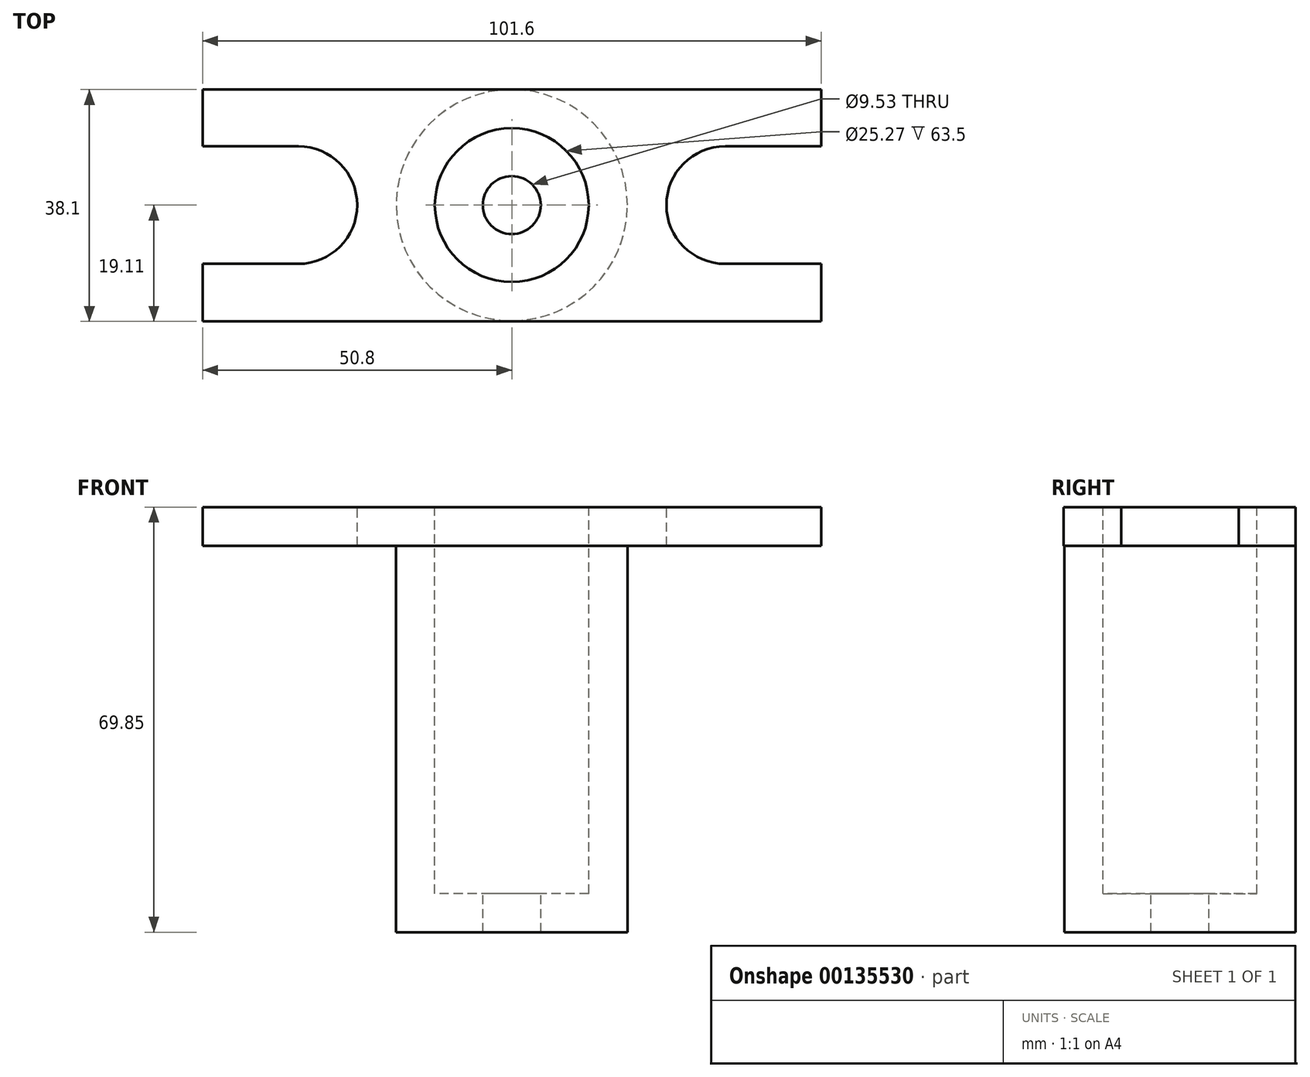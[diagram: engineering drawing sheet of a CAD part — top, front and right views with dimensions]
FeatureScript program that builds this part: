
annotation { "Feature Type Name" : "Feature", "Feature Type Description" : "" }
export const myFeature = defineFeature(function(context is Context, id is Id, definition is map)
    precondition{}
    {
        {
            var Q0;
            Q0=qCreatedBy(makeId("Front.planeOp"),FACE);
            var sketch = newSketch(context, id + "F0", { "sketchPlane" : qUnion([Q0])});
            skLineSegment(sketch, "E0", {"start": v(4.76, 0) * mm, "end": v(18.99, 0) * mm});
            skLineSegment(sketch, "E1", {"start": v(18.99, 0) * mm, "end": v(18.99, 63.5) * mm});
            skLineSegment(sketch, "E2", {"start": v(18.99, 63.5) * mm, "end": v(12.64, 63.5) * mm});
            skLineSegment(sketch, "E3", {"start": v(12.64, 63.5) * mm, "end": v(12.64, 6.35) * mm});
            skLineSegment(sketch, "E4", {"start": v(12.64, 6.35) * mm, "end": v(4.76, 6.35) * mm});
            skLineSegment(sketch, "E5", {"start": v(4.76, 6.35) * mm, "end": v(4.76, 0) * mm});
            skLineSegment(sketch, "E6", {"start": v(0, 37.58) * mm, "end": v(0, -25.7) * mm, "construction": true});
            skSolve(sketch);
        }
        {
            var Q0;
            Q0=makeQuery(id+"F0.imprint","IMPRINT",FACE,{"disambiguationData":[TD([[makeQuery(id+"F0.imprint","IMPRINT",EDGE,{"derivedFrom":sQuery(id+"F0.wireOp",EDGE,"E0")}),1.0]])]});
            var Q1;
            Q1=sQuery(id+"F0.wireOp",EDGE,"E6");
            revolve(context, id + "F1", {"entities" : qUnion([Q0]), "axis" : qUnion([Q1]), "revolveType" : RevolveType.FULL});
        }
        {
            var Q0;
            Q0=makeQuery(id+"F1.opRevolve","SWEPT_FACE",FACE,{"disambiguationData":[OSD([sQuery(id+"F0.wireOp",EDGE,"E2")])]});
            var sketch = newSketch(context, id + "F2", { "sketchPlane" : qUnion([Q0])});
            skLineSegment(sketch, "E7", {"start": v(0, -18.99) * mm, "end": v(0, 49.89) * mm});
            skLineSegment(sketch, "E8", {"start": v(0, 49.89) * mm, "end": v(0, 18.99) * mm, "construction": true});
            skLineSegment(sketch, "E9.bottom", {"start": v(-50.8, 18.99) * mm, "end": v(50.8, 18.99) * mm});
            skLineSegment(sketch, "E9.top", {"start": v(-50.8, -19.11) * mm, "end": v(50.8, -19.11) * mm});
            skLineSegment(sketch, "E9.left", {"start": v(-50.8, 18.99) * mm, "end": v(-50.8, -19.11) * mm});
            skLineSegment(sketch, "E9.right", {"start": v(50.8, 18.99) * mm, "end": v(50.8, -19.11) * mm});
            skCircle(sketch, "E10", {"center": v(0, 0) * mm, "radius": 12.64 * mm});
            skSolve(sketch);
        }
        {
            var Q0;
            Q0=makeQuery(id+"F2.imprint","IMPRINT",FACE,{"disambiguationData":[TD([[makeQuery(id+"F2.imprint","IMPRINT",EDGE,{"derivedFrom":sQuery(id+"F2.wireOp",EDGE,"E9.top")}),1.0]])]});
            var Q1;
            {var subQ0=sQuery(id+"F2.wireOp",EDGE,"E10");var subQ1=sQuery(id+"F2.wireOp",EDGE,"E7");var subQ2=makeQuery(id+"F2.imprint","INTERSECT",VERTEX,{"disambiguationData":[OD(0.0)],"derivedFrom":[subQ1,subQ0]});Q1=makeQuery(id+"F2.imprint","IMPRINT",FACE,{"disambiguationData":[TD([[makeQuery(id+"F2.imprint","IMPRINT",EDGE,{"disambiguationData":[TD([[subQ2,-1.0]])],"derivedFrom":subQ0}),-1.0]])]});}
            var Q2;
            {var subQ0=sQuery(id+"F2.wireOp",EDGE,"E10");var subQ1=sQuery(id+"F2.wireOp",EDGE,"E7");var subQ2=makeQuery(id+"F2.imprint","INTERSECT",VERTEX,{"disambiguationData":[OD(0.0)],"derivedFrom":[subQ1,subQ0]});Q2=makeQuery(id+"F2.imprint","IMPRINT",FACE,{"disambiguationData":[TD([[makeQuery(id+"F2.imprint","IMPRINT",EDGE,{"disambiguationData":[TD([[subQ2,1.0]])],"derivedFrom":subQ0}),-1.0]])]});}
            extrude(context, id + "F3", {"entities" : qUnion([Q0, Q1, Q2]), "operationType" : NewBodyOperationType.ADD, "depth" : 6.35 * mm});
        }
        {
            var Q0;
            Q0=makeQuery(id+"F3.opExtrude","CAP_FACE",FACE,{"disambiguationData":[OSD([sQuery(id+"F2.wireOp",EDGE,"E9.bottom"),sQuery(id+"F2.wireOp",EDGE,"E9.top"),sQuery(id+"F2.wireOp",EDGE,"E9.left"),sQuery(id+"F2.wireOp",EDGE,"E9.right"),sQuery(id+"F2.wireOp",EDGE,"E10")])],"isStart":false});
            var sketch = newSketch(context, id + "F4", { "sketchPlane" : qUnion([Q0])});
            skLineSegment(sketch, "E11", {"start": v(-35.05, -9.65) * mm, "end": v(-50.8, -9.65) * mm});
            skLineSegment(sketch, "E12", {"start": v(-50.8, -9.65) * mm, "end": v(-50.8, 9.65) * mm});
            skLineSegment(sketch, "E13", {"start": v(-50.8, 9.65) * mm, "end": v(-35.05, 9.65) * mm});
            skLineSegment(sketch, "E14", {"start": v(35.05, -9.65) * mm, "end": v(50.8, -9.65) * mm});
            skLineSegment(sketch, "E15", {"start": v(50.8, -9.65) * mm, "end": v(50.8, 9.65) * mm});
            skLineSegment(sketch, "E16", {"start": v(50.8, 9.65) * mm, "end": v(35.05, 9.65) * mm});
            skArc(sketch, "E17", {"start": v(35.05, 9.65) * mm, "mid": v(25.4, 0) * mm, "end": v(35.05, -9.65) * mm});
            skArc(sketch, "E18", {"start": v(-35.05, -9.65) * mm, "mid": v(-25.4, 0) * mm, "end": v(-35.05, 9.65) * mm});
            skLineSegment(sketch, "E19", {"start": v(0, -32.69) * mm, "end": v(0, 37.38) * mm, "construction": true});
            skPoint(sketch, "E19.endSnap0", {"position": v(0, 18.99) * mm});
            skLineSegment(sketch, "E20", {"start": v(35.05, -19.11) * mm, "end": v(35.05, 33.03) * mm, "construction": true});
            skLineSegment(sketch, "E21", {"start": v(-35.05, -19.11) * mm, "end": v(-35.05, 27.76) * mm, "construction": true});
            skLineSegment(sketch, "E22", {"start": v(-50.8, -19.11) * mm, "end": v(-50.8, 18.99) * mm});
            skLineSegment(sketch, "E23", {"start": v(-50.8, 0) * mm, "end": v(-50.8, 0) * mm});
            skPoint(sketch, "E23.endSnap0", {"position": v(-50.8, 0) * mm});
            skLineSegment(sketch, "E24", {"start": v(-61.4, 0) * mm, "end": v(54.13, 0) * mm, "construction": true});
            skSolve(sketch);
        }
        {
            var Q0;
            {var subQ0=sQuery(id+"F4.wireOp",EDGE,"E11");Q0=makeQuery(id+"F4.imprint","IMPRINT",FACE,{"disambiguationData":[TD([[makeQuery(id+"F4.imprint","IMPRINT",EDGE,{"derivedFrom":subQ0}),-1.0]])]});}
            var Q1;
            Q1=makeQuery(id+"F4.imprint","IMPRINT",FACE,{"disambiguationData":[TD([[makeQuery(id+"F4.imprint","IMPRINT",EDGE,{"derivedFrom":sQuery(id+"F4.wireOp",EDGE,"E14")}),1.0]])]});
            extrude(context, id + "F5", {"entities" : qUnion([Q0, Q1]), "operationType" : NewBodyOperationType.REMOVE, "oppositeDirection" : true, "depth" : 25.4 * mm});
        }
    });
